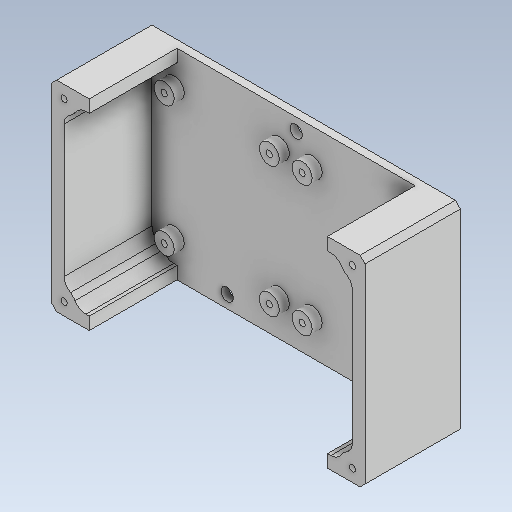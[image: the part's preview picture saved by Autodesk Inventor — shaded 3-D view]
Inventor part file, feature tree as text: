
AUTODESK INVENTOR PART (.ipt)
format: ipt  version: 2020 (Build 240168000, 168)  size: 306,176 bytes
history: native  units: mm
features: sketch x8, reference x8, extrude x6, other x4, hole x2, projected_geometry x2, fillet x1, chamfer x1
ambient origin geometry x8: Origin, YZ Plane, XZ Plane, XY Plane, X Axis, Y Axis, Z Axis, Center Point
bodies: Solid1 (feature_tree)
feature tree (32):
  extrude  "Extrusion1"  Depth=80.0mm
  extrude  "Extrusion2"  Depth=5.0mm
  extrude  "Extrusion3"  Depth=3.0mm
  extrude  "Extrusion4"  Depth=15.0mm
  extrude  "Extrusion5"  Depth=2.5mm
  fillet  "Fillet1"  Radius=2.5mm
  hole  "Hole1"  [1 undecoded]
  extrude  "Extrusion6"  Depth=5.0mm
  chamfer  "Chamfer1"  Distance=5.0mm
  hole  "Hole2"  [1 undecoded]
  sketch  "Sketch1"  dims[d0=125.0mm d1=80.0mm]
  sketch  "Sketch2"  dims[d2=3.0mm d3=0.0mm d4=5.0mm]
  projected_geometry  "Projected Loop1"
  sketch  "Sketch3"  dims[d5=35.0mm d6=0.0mm d7=3.0mm]
  sketch  "Sketch4"  dims[d8=15.0mm d9=15.0mm]
  sketch  "Sketch5"  dims[d10=0.0mm d11=0.0mm d12=2.5mm d13=2.5mm]
  sketch  "Sketch6"  dims[d14=5.0mm d15=5.0mm]
  reference  "Reference2"
  reference  "Reference3"
  reference  "Reference4"
  reference  "Reference5"
  reference  "Reference6"
  reference  "Reference7"
  reference  "Reference8"
  reference  "Reference9"
  sketch  "Sketch7"  dims[d16=5.0mm d17=5.0mm]
  projected_geometry  "Projected Loop2"
  sketch  "Sketch8"  dims[d18=5.0mm d19=5.0mm d20=5.0mm d21=5.0mm d22=35.0mm d23=0.0mm d24=0.0mm d25=0.0mm d26=5.0mm d27=2.5mm d28=6.0mm d29=4.0mm d30=2.0mm d31=90.0deg d32=8.0mm d33=20.594885mm d34=8.0mm d35=4.0mm d36=0.0mm d37=2.0mm d38=2.0mm d39=45.0deg d40=20.0mm d41=20.0mm d42=5.0mm d43=5.0mm d44=6.0mm d45=4.0mm d46=2.0mm d47=90.0deg d48=8.0mm d49=20.594885mm d50=5.0mm]
  parser-record x1  (decoder bookkeeping rows leaked as tree rows — omitted from the tree; the rows remain in map.json)
  other  "10-06-04 COntroler Bed.iam"
  other  "MOSFET_Step:2"
  other  "MOSFET_Step:1"
note: 2 required parameter values undecoded (feature->parameter linkage not recoverable at this tier; creation-order binding heuristic only, values carry confidence <= 0.55)
note: 1 file-system path scrubbed to <path> (originals preserved in map.json)
